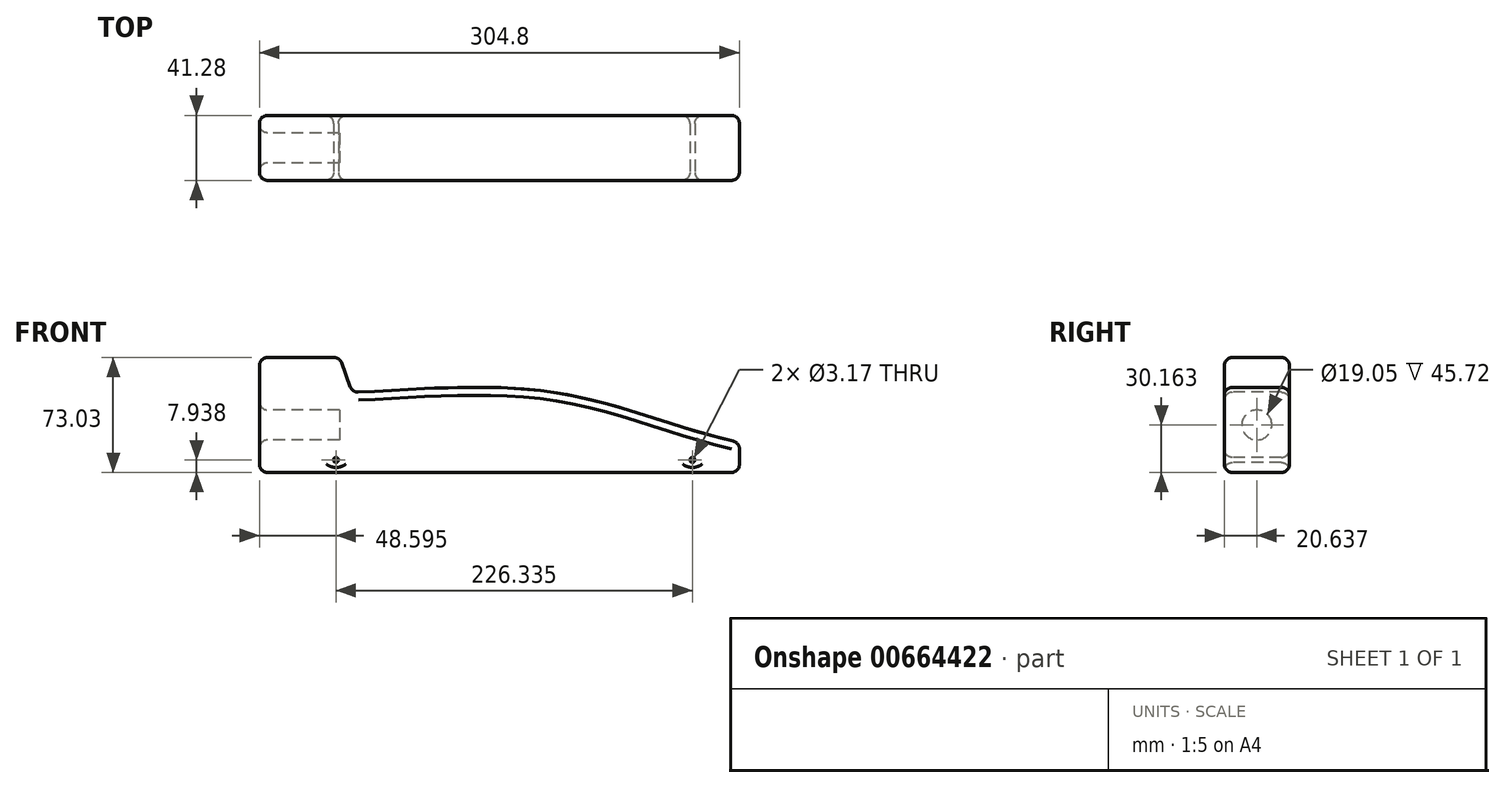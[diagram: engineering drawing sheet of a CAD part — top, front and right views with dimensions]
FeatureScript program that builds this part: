
annotation { "Feature Type Name" : "Feature", "Feature Type Description" : "" }
export const myFeature = defineFeature(function(context is Context, id is Id, definition is map)
    precondition{}
    {
        {
            var Q0;
            Q0=qCreatedBy(makeId("Front.planeOp"),FACE);
            var sketch = newSketch(context, id + "F0", { "sketchPlane" : qUnion([Q0])});
            skLineSegment(sketch, "E0", {"start": v(0, 0) * mm, "end": v(304.8, 0) * mm});
            skLineSegment(sketch, "E1", {"start": v(304.8, 0) * mm, "end": v(304.8, 19.05) * mm});
            skLineSegment(sketch, "E2", {"start": v(0, 73.03) * mm, "end": v(0, 0) * mm});
            skLineSegment(sketch, "E3", {"start": v(0, 73.03) * mm, "end": v(50.8, 73.03) * mm});
            skLineSegment(sketch, "E4", {"start": v(50.8, 73.03) * mm, "end": v(58.96, 50.8) * mm});
            skFitSpline(sketch, "E5", {"points": [v(58.96, 50.8) * mm, v(187.12, 50.8) * mm, v(304.8, 19.05) * mm], "startDerivative": vector(231.38, 9.9) * mm, "endDerivative": vector(233.35, -50.15) * mm});
            skSolve(sketch);
        }
        {
            var Q0;
            Q0=makeQuery(id+"F0.imprint","IMPRINT",FACE,{"disambiguationData":[TD([[makeQuery(id+"F0.imprint","IMPRINT",EDGE,{"derivedFrom":sQuery(id+"F0.wireOp",EDGE,"E0")}),1.0]])]});
            extrude(context, id + "F1", {"entities" : qUnion([Q0]), "oppositeDirection" : true, "depth" : 41.27 * mm, "offsetDistance" : 25.4 * mm});
        }
        {
            var Q0;
            Q0=makeQuery(id+"F1.opExtrude","SWEPT_FACE",FACE,{"disambiguationData":[OSD([sQuery(id+"F0.wireOp",EDGE,"E2")])]});
            var sketch = newSketch(context, id + "F2", { "sketchPlane" : qUnion([Q0])});
            skCircle(sketch, "E6", {"center": v(-20.64, 30.16) * mm, "radius": 9.53 * mm});
            skSolve(sketch);
        }
        {
            var Q0;
            Q0=makeQuery(id+"F2.imprint","IMPRINT",FACE,{"disambiguationData":[TD([[makeQuery(id+"F2.imprint","IMPRINT",EDGE,{"derivedFrom":sQuery(id+"F2.wireOp",EDGE,"E6")}),1.0]])]});
            extrude(context, id + "F3", {"entities" : qUnion([Q0]), "operationType" : NewBodyOperationType.REMOVE, "oppositeDirection" : true, "depth" : 50.8 * mm, "offsetDistance" : 25.4 * mm});
        }
        {
            var Q0;
            Q0=makeQuery(id+"F1.opExtrude","CAP_FACE",FACE,{"disambiguationData":[OSD([sQuery(id+"F0.wireOp",EDGE,"E0"),sQuery(id+"F0.wireOp",EDGE,"E1"),sQuery(id+"F0.wireOp",EDGE,"X4BVIAdR-dthh-fWhn-U1zp-n8XLNdKa0UT1"),sQuery(id+"F0.wireOp",EDGE,"E2")])],"isStart":true});
            var sketch = newSketch(context, id + "F4", { "sketchPlane" : qUnion([Q0])});
            skSolve(sketch);
        }
        {
            var Q0;
            Q0=makeQuery(id+"F4.imprint","IMPRINT",FACE,{"disambiguationData":[TD([[makeQuery(id+"F4.imprint","IMPRINT",EDGE,{"derivedFrom":makeQuery(id+"F1.opExtrude","CAP_EDGE",EDGE,{"disambiguationData":[OSD([sQuery(id+"F0.wireOp",EDGE,"E0")])],"isStart":true})}),1.0]])]});
            var sketch = newSketch(context, id + "F5", { "sketchPlane" : qUnion([Q0])});
            skCircle(sketch, "E7", {"center": v(274.93, 7.94) * mm, "radius": 1.59 * mm});
            skCircle(sketch, "E8", {"center": v(48.6, 7.94) * mm, "radius": 1.59 * mm});
            skSolve(sketch);
        }
        {
            var Q0;
            Q0=makeQuery(id+"F5.imprint","IMPRINT",FACE,{"disambiguationData":[TD([[makeQuery(id+"F5.imprint","IMPRINT",EDGE,{"derivedFrom":sQuery(id+"F5.wireOp",EDGE,"E7")}),1.0]])]});
            var Q1;
            Q1=makeQuery(id+"F5.imprint","IMPRINT",FACE,{"disambiguationData":[TD([[makeQuery(id+"F5.imprint","IMPRINT",EDGE,{"derivedFrom":sQuery(id+"F5.wireOp",EDGE,"E8")}),1.0]])]});
            extrude(context, id + "F6", {"entities" : qUnion([Q0, Q1]), "operationType" : NewBodyOperationType.REMOVE, "oppositeDirection" : true, "depth" : 50.8 * mm, "offsetDistance" : 25.4 * mm});
        }
        {
            var Q0;
            Q0=makeQuery(id+"F1.opExtrude","SWEPT_FACE",FACE,{"disambiguationData":[OSD([sQuery(id+"F0.wireOp",EDGE,"E5")])]});
            var Q1;
            Q1=makeQuery(id+"F1.opExtrude","CAP_FACE",FACE,{"disambiguationData":[OSD([sQuery(id+"F0.wireOp",EDGE,"E0"),sQuery(id+"F0.wireOp",EDGE,"E1"),sQuery(id+"F0.wireOp",EDGE,"E2"),sQuery(id+"F0.wireOp",EDGE,"E3"),sQuery(id+"F0.wireOp",EDGE,"E4"),sQuery(id+"F0.wireOp",EDGE,"E5")])],"isStart":true});
            var Q2;
            Q2=makeQuery(id+"F1.opExtrude","SWEPT_FACE",FACE,{"disambiguationData":[OSD([sQuery(id+"F0.wireOp",EDGE,"E3")])]});
            var Q3;
            Q3=makeQuery(id+"F1.opExtrude","SWEPT_FACE",FACE,{"disambiguationData":[OSD([sQuery(id+"F0.wireOp",EDGE,"E1")])]});
            var Q4;
            Q4=makeQuery(id+"F1.opExtrude","SWEPT_FACE",FACE,{"disambiguationData":[OSD([sQuery(id+"F0.wireOp",EDGE,"E2")])]});
            var Q5;
            Q5=makeQuery(id+"F1.opExtrude","CAP_FACE",FACE,{"disambiguationData":[OSD([sQuery(id+"F0.wireOp",EDGE,"E0"),sQuery(id+"F0.wireOp",EDGE,"E1"),sQuery(id+"F0.wireOp",EDGE,"E2"),sQuery(id+"F0.wireOp",EDGE,"E3"),sQuery(id+"F0.wireOp",EDGE,"E4"),sQuery(id+"F0.wireOp",EDGE,"E5")])],"isStart":false});
            fillet(context, id + "F7", {"entities" : qUnion([Q0, Q1, Q2, Q3, Q4, Q5]), "radius" : 5.08 * mm, "tangentPropagation" : true, "allowEdgeOverflow" : false});
        }
    });
